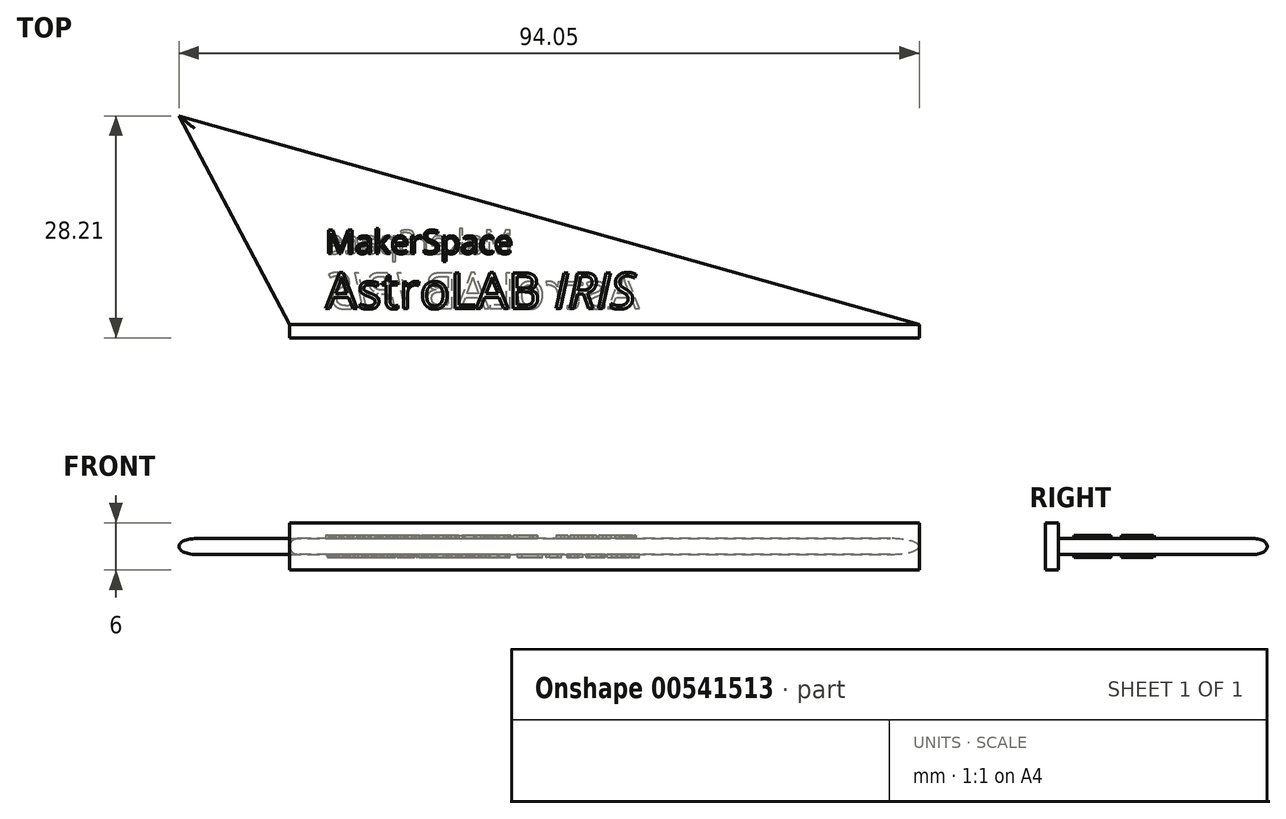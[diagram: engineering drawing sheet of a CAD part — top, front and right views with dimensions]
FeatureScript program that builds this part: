
annotation { "Feature Type Name" : "Feature", "Feature Type Description" : "" }
export const myFeature = defineFeature(function(context is Context, id is Id, definition is map)
    precondition{}
    {
        {
            var Q0;
            Q0=qCreatedBy(makeId("Front.planeOp"),FACE);
            var sketch = newSketch(context, id + "F0", { "sketchPlane" : qUnion([Q0])});
            skLineSegment(sketch, "E0.bottom", {"start": v(-40, 3) * mm, "end": v(40, 3) * mm});
            skLineSegment(sketch, "E0.top", {"start": v(-40, -3) * mm, "end": v(40, -3) * mm});
            skLineSegment(sketch, "E0.left", {"start": v(-40, 3) * mm, "end": v(-40, -3) * mm});
            skLineSegment(sketch, "E0.right", {"start": v(40, 3) * mm, "end": v(40, -3) * mm});
            skPoint(sketch, "E0.middle", {"position": v(0, 0) * mm});
            skSolve(sketch);
        }
        {
            var Q0;
            Q0=qCreatedBy(makeId("Front.planeOp"),FACE);
            var sketch = newSketch(context, id + "F1", { "sketchPlane" : qUnion([Q0])});
            skLineSegment(sketch, "E1.bottom", {"start": v(-40, 0.85) * mm, "end": v(40, 0.85) * mm});
            skLineSegment(sketch, "E1.top", {"start": v(-40, -0.85) * mm, "end": v(40, -0.85) * mm});
            skLineSegment(sketch, "E1.left", {"start": v(-40, 0.85) * mm, "end": v(-40, -0.85) * mm});
            skLineSegment(sketch, "E1.right", {"start": v(40, 0.85) * mm, "end": v(40, -0.85) * mm});
            skPoint(sketch, "E1.middle", {"position": v(0, 0) * mm});
            skSolve(sketch);
        }
        {
            var Q0;
            Q0=qCreatedBy(makeId("Top.planeOp"),FACE);
            var sketch = newSketch(context, id + "F2", { "sketchPlane" : qUnion([Q0])});
            skLineSegment(sketch, "E2", {"start": v(40, 0) * mm, "end": v(-40, 0) * mm});
            skLineSegment(sketch, "E3", {"start": v(-40, 0) * mm, "end": v(-40, 26.5) * mm, "construction": true});
            skLineSegment(sketch, "E4", {"start": v(-40, 26.5) * mm, "end": v(-54.05, 26.5) * mm, "construction": true});
            skLineSegment(sketch, "E5", {"start": v(-54.05, 26.5) * mm, "end": v(-40, 0) * mm});
            skLineSegment(sketch, "E6", {"start": v(-54.05, 26.5) * mm, "end": v(40, 0) * mm});
            skSolve(sketch);
        }
        {
            var Q0;
            Q0=qSketchRegion(id+"F0",true);
            extrude(context, id + "F3", {"entities" : qUnion([Q0]), "depth" : 1.7 * mm});
        }
        {
            var Q0;
            Q0=makeQuery(id+"F2.imprint","IMPRINT",FACE,{"disambiguationData":[TD([[makeQuery(id+"F2.imprint","IMPRINT",EDGE,{"derivedFrom":sQuery(id+"F2.wireOp",EDGE,"E2")}),-1.0]])]});
            extrude(context, id + "F4", {"entities" : qUnion([Q0]), "operationType" : NewBodyOperationType.ADD, "endBound" : BoundingType.SYMMETRIC, "depth" : 2 * mm});
        }
        {
            var Q0;
            Q0=makeQuery(id+"F4.opExtrude","CAP_EDGE",EDGE,{"disambiguationData":[OSD([sQuery(id+"F2.wireOp",EDGE,"E6")])],"isStart":false});
            var Q1;
            Q1=makeQuery(id+"F4.opExtrude","CAP_EDGE",EDGE,{"disambiguationData":[OSD([sQuery(id+"F2.wireOp",EDGE,"E6")])],"isStart":true});
            var Q2;
            Q2=makeQuery(id+"F4.opExtrude","CAP_EDGE",EDGE,{"disambiguationData":[OSD([sQuery(id+"F2.wireOp",EDGE,"E5")])],"isStart":false});
            var Q3;
            Q3=makeQuery(id+"F4.opExtrude","CAP_EDGE",EDGE,{"disambiguationData":[OSD([sQuery(id+"F2.wireOp",EDGE,"E5")])],"isStart":true});
            fillet(context, id + "F5", {"entities" : qUnion([Q0, Q1, Q2, Q3]), "radius" : 1 * mm, "tangentPropagation" : true, "allowEdgeOverflow" : false});
        }
        {
            var Q0;
            Q0=makeQuery(id+"F4.opExtrude","CAP_FACE",FACE,{"disambiguationData":[OSD([sQuery(id+"F2.wireOp",EDGE,"E2"),sQuery(id+"F2.wireOp",EDGE,"E5"),sQuery(id+"F2.wireOp",EDGE,"E6")])],"isStart":false});
            var sketch = newSketch(context, id + "F6", { "sketchPlane" : qUnion([Q0])});
            skText(sketch, "E7", { "text": "MakerSpace", "fontName": "OpenSans-Regular.ttf"});
            skLineSegment(sketch, "E8", {"start": v(-35.43, 2) * mm, "end": v(-35.43, 12) * mm, "construction": true});
            skLineSegment(sketch, "E9", {"start": v(-35.43, 2) * mm, "end": v(-35.43, 0) * mm, "construction": true});
            skLineSegment(sketch, "E10", {"start": v(-35.43, 2) * mm, "end": v(-39.93, 2) * mm, "construction": true});
            skText(sketch, "E11", { "text": "AstroLAB ", "fontName": "OpenSans-Regular.ttf"});
            skText(sketch, "E12", { "text": " IRIS", "fontName": "OpenSans-Italic.ttf"});
            const initialGuessF6  = {"E7": [-0.03543, 0.009, 1, 0, 0.003], "E11": [-0.03543, 0.002, 1, 0, 0.0046], "E12": [-0.00805, 0.002, 1, 0, 0.0046]};
            skSetInitialGuess(sketch, initialGuessF6);
            skSolve(sketch);
        }
        {
            var Q0;
            Q0=makeQuery(id+"F4.opExtrude","CAP_FACE",FACE,{"disambiguationData":[OSD([sQuery(id+"F2.wireOp",EDGE,"E2"),sQuery(id+"F2.wireOp",EDGE,"E5"),sQuery(id+"F2.wireOp",EDGE,"E6")])],"isStart":true});
            var sketch = newSketch(context, id + "F7", { "sketchPlane" : qUnion([Q0])});
            skLineSegment(sketch, "E13", {"start": v(-35.43, 0) * mm, "end": v(-35.43, -2) * mm, "construction": true});
            skLineSegment(sketch, "E14", {"start": v(-35.43, -2) * mm, "end": v(-39.93, -2) * mm, "construction": true});
            skLineSegment(sketch, "E15", {"start": v(-35.43, -2) * mm, "end": v(-35.43, -12) * mm, "construction": true});
            skText(sketch, "E16", { "text": "MakerSpace", "fontName": "OpenSans-Regular.ttf"});
            skText(sketch, "E17", { "text": " IRIS", "fontName": "OpenSans-Italic.ttf"});
            skText(sketch, "E18", { "text": "AstroLAB", "fontName": "OpenSans-Regular.ttf"});
            const initialGuessF7  = {"E16": [-0.0116, -0.009, -1, 0, 0.003], "E17": [-0.02293, -0.002, -1, 0, 0.0046], "E18": [0.00445, -0.002, -1, 0, 0.0046]};
            skSetInitialGuess(sketch, initialGuessF7);
            skSolve(sketch);
        }
        {
            var Q0;
            Q0=qSketchRegion(id+"F7",true);
            extrude(context, id + "F8", {"entities" : qUnion([Q0]), "operationType" : NewBodyOperationType.ADD, "depth" : 0.4 * mm});
        }
        {
            var Q0;
            Q0=qSketchRegion(id+"F6",true);
            extrude(context, id + "F9", {"entities" : qUnion([Q0]), "operationType" : NewBodyOperationType.ADD, "depth" : .4 * mm});
        }
    });
